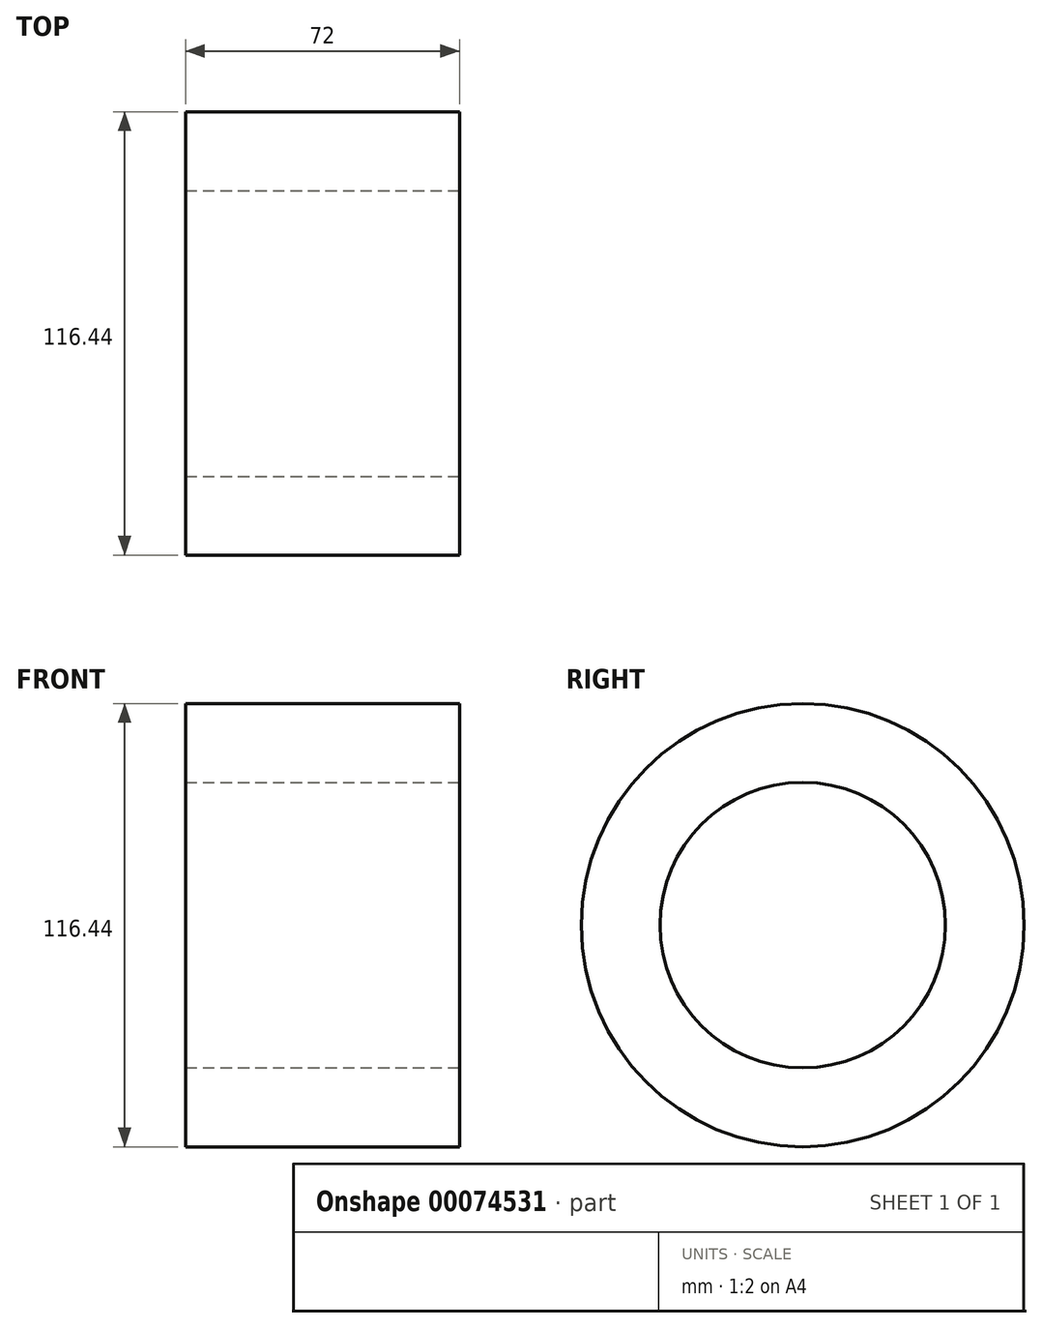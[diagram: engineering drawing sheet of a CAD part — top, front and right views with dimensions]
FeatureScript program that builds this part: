
annotation { "Feature Type Name" : "Feature", "Feature Type Description" : "" }
export const myFeature = defineFeature(function(context is Context, id is Id, definition is map)
    precondition{}
    {
        {
            var Q0;
            Q0=qCreatedBy(makeId("Front.planeOp"),FACE);
            var sketch = newSketch(context, id + "F0", { "sketchPlane" : qUnion([Q0])});
            skLineSegment(sketch, "E0", {"start": v(0, 0) * mm, "end": v(0, 58.22) * mm});
            skLineSegment(sketch, "E1", {"start": v(0, 58.22) * mm, "end": v(72, 58.22) * mm});
            skLineSegment(sketch, "E2", {"start": v(72, 58.22) * mm, "end": v(72, 0) * mm});
            skLineSegment(sketch, "E3", {"start": v(72, 0) * mm, "end": v(0, 0) * mm});
            skLineSegment(sketch, "E4", {"start": v(0, 37.5) * mm, "end": v(72, 37.5) * mm});
            skSolve(sketch);
        }
        {
            var Q0;
            {var subQ0=sQuery(id+"F0.wireOp",EDGE,"E1");Q0=makeQuery(id+"F0.imprint","IMPRINT",FACE,{"disambiguationData":[TD([[makeQuery(id+"F0.imprint","IMPRINT",EDGE,{"derivedFrom":subQ0}),-1.0]])]});}
            var Q1;
            Q1=sQuery(id+"F0.wireOp",EDGE,"E3");
            revolve(context, id + "F1", {"entities" : qUnion([Q0]), "axis" : qUnion([Q1]), "revolveType" : RevolveType.FULL});
        }
    });
